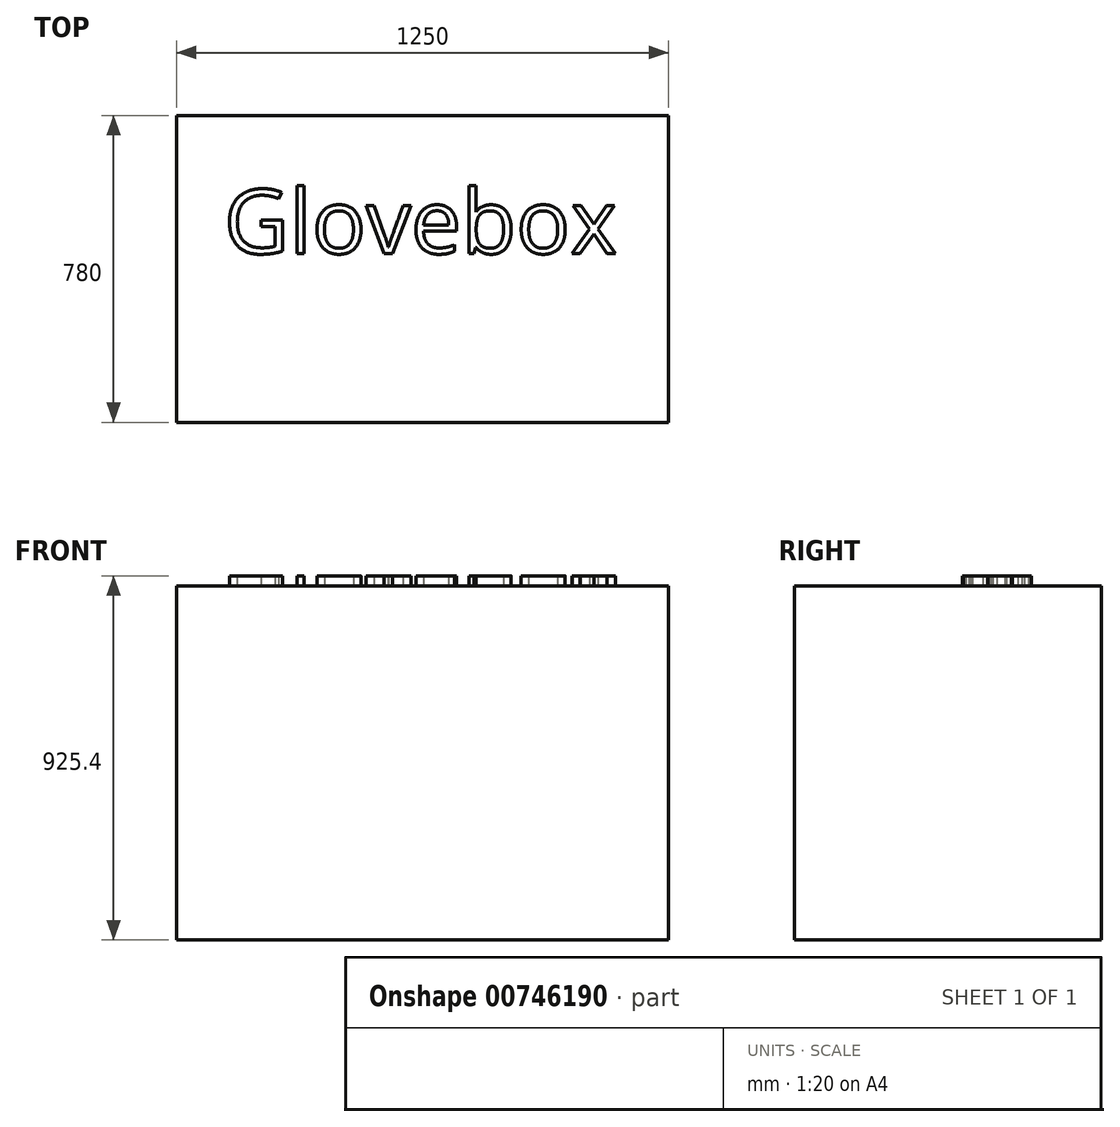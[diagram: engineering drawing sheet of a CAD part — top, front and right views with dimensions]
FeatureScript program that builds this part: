
annotation { "Feature Type Name" : "Feature", "Feature Type Description" : "" }
export const myFeature = defineFeature(function(context is Context, id is Id, definition is map)
    precondition{}
    {
        {
            var Q0;
            Q0=qCreatedBy(makeId("Top.planeOp"),FACE);
            var sketch = newSketch(context, id + "F0", { "sketchPlane" : qUnion([Q0])});
            skLineSegment(sketch, "E0.bottom", {"start": v(625, -390) * mm, "end": v(-625, -390) * mm});
            skLineSegment(sketch, "E0.top", {"start": v(625, 390) * mm, "end": v(-625, 390) * mm});
            skLineSegment(sketch, "E0.left", {"start": v(625, -390) * mm, "end": v(625, 390) * mm});
            skLineSegment(sketch, "E0.right", {"start": v(-625, -390) * mm, "end": v(-625, 390) * mm});
            skPoint(sketch, "E0.middle", {"position": v(0, 0) * mm});
            skSolve(sketch);
        }
        {
            var Q0;
            Q0=makeQuery(id+"F0.imprint","IMPRINT",FACE,{"disambiguationData":[TD([[makeQuery(id+"F0.imprint","IMPRINT",EDGE,{"derivedFrom":sQuery(id+"F0.wireOp",EDGE,"E0.bottom")}),-1.0]])]});
            extrude(context, id + "F1", {"entities" : qUnion([Q0]), "depth" : 900 * mm, "offsetDistance" : 25.4 * mm});
        }
        {
            var Q0;
            Q0=makeQuery(id+"F1.opExtrude","CAP_FACE",FACE,{"disambiguationData":[OSD([sQuery(id+"F0.wireOp",EDGE,"E0.bottom"),sQuery(id+"F0.wireOp",EDGE,"E0.top"),sQuery(id+"F0.wireOp",EDGE,"E0.left"),sQuery(id+"F0.wireOp",EDGE,"E0.right")])],"isStart":false});
            var sketch = newSketch(context, id + "F2", { "sketchPlane" : qUnion([Q0])});
            skText(sketch, "E1", { "text": "Glovebox", "fontName": "OpenSans-Regular.ttf"});
            const initialGuessF2  = {"E1": [-0.50463, 0.03911, 1, 0, 0.16394]};
            skSetInitialGuess(sketch, initialGuessF2);
            skSolve(sketch);
        }
        {
            var Q0;
            Q0 = qSketchRegion(id + "F2", true);
            extrude(context, id + "F3", {"entities" : qUnion([Q0]), "operationType" : NewBodyOperationType.ADD, "depth" : 25.4 * mm, "offsetDistance" : 25.4 * mm});
        }
    });
